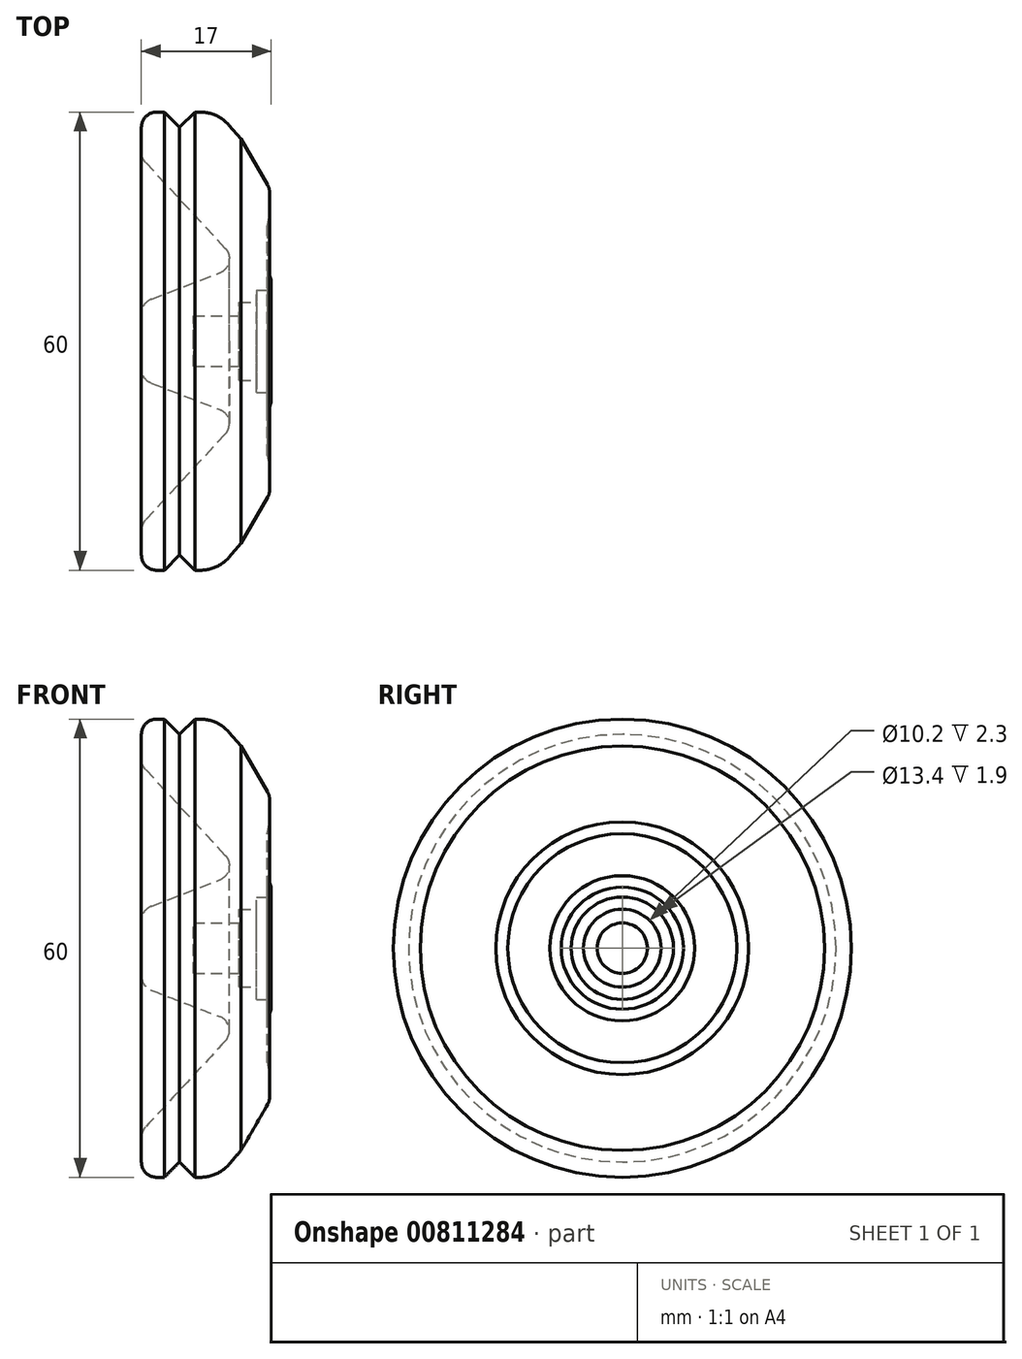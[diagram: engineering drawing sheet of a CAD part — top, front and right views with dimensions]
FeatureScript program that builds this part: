
annotation { "Feature Type Name" : "Feature", "Feature Type Description" : "" }
export const myFeature = defineFeature(function(context is Context, id is Id, definition is map)
    precondition{}
    {
        {
            var Q0;
            Q0=qCreatedBy(makeId("Front.planeOp"),FACE);
            var sketch = newSketch(context, id + "F0", { "sketchPlane" : qUnion([Q0])});
            skLineSegment(sketch, "E0", {"start": v(2, 30) * mm, "end": v(3, 30) * mm});
            skLineSegment(sketch, "E1", {"start": v(3, 30) * mm, "end": v(5, 28) * mm});
            skLineSegment(sketch, "E2", {"start": v(5, 28) * mm, "end": v(7, 30) * mm});
            skLineSegment(sketch, "E3", {"start": v(15.1, 5.1) * mm, "end": v(12.8, 5.1) * mm});
            skLineSegment(sketch, "E4", {"start": v(12.8, 5.1) * mm, "end": v(12.8, 3.3) * mm});
            skLineSegment(sketch, "E5", {"start": v(12.8, 3.3) * mm, "end": v(6.8, 3.3) * mm});
            skLineSegment(sketch, "E6", {"start": v(6.8, 3.3) * mm, "end": v(6.8, 0) * mm});
            skLineSegment(sketch, "E7", {"start": v(6.8, 0) * mm, "end": v(0, 0) * mm});
            skPoint(sketch, "E8.visualSharp", {"position": v(0, 30) * mm});
            skLineSegment(sketch, "E9", {"start": v(15.1, 5.1) * mm, "end": v(15.1, 6.7) * mm});
            skLineSegment(sketch, "E10", {"start": v(15.1, 6.7) * mm, "end": v(17, 6.7) * mm});
            skLineSegment(sketch, "E11", {"start": v(17, 6.7) * mm, "end": v(17, 8) * mm});
            skLineSegment(sketch, "E12", {"start": v(16.5, 15) * mm, "end": v(16.5, 9.5) * mm});
            skLineSegment(sketch, "E13", {"start": v(16.5, 9.5) * mm, "end": v(17, 8) * mm});
            skLineSegment(sketch, "E14", {"start": v(0, 3.63) * mm, "end": v(0, 0) * mm});
            skLineSegment(sketch, "E15", {"start": v(16.8, 16.55) * mm, "end": v(16.5, 15) * mm});
            skPoint(sketch, "E16.visualSharp", {"position": v(16.8, 20) * mm});
            skPoint(sketch, "E17.visualSharp", {"position": v(0, 24) * mm});
            skLineSegment(sketch, "E18", {"start": v(7, 30) * mm, "end": v(7.72, 30) * mm});
            skLineSegment(sketch, "E19", {"start": v(11.5, 28.28) * mm, "end": v(13.06, 26.48) * mm});
            skLineSegment(sketch, "E20", {"start": v(13.06, 26.48) * mm, "end": v(16.53, 20.46) * mm});
            skLineSegment(sketch, "E21", {"start": v(16.8, 16.55) * mm, "end": v(16.8, 19.46) * mm});
            skPoint(sketch, "E22.visualSharp", {"position": v(10, 30) * mm});
            skLineSegment(sketch, "E23", {"start": v(0, 28) * mm, "end": v(0, 24.79) * mm});
            skPoint(sketch, "E24.visualSharp", {"position": v(0, 5) * mm});
            skPoint(sketch, "E25.visualSharp", {"position": v(13, 10) * mm});
            skLineSegment(sketch, "E26", {"start": v(10.99, 12.17) * mm, "end": v(0.53, 23.42) * mm});
            skLineSegment(sketch, "E27", {"start": v(1.28, 5.5) * mm, "end": v(10.24, 8.94) * mm});
            skArc(sketch, "E28.filletArc", {"start": v(2, 30) * mm, "mid": v(0.59, 29.41) * mm, "end": v(0, 28) * mm});
            skArc(sketch, "E29.filletArc", {"start": v(11.5, 28.28) * mm, "mid": v(9.8, 29.55) * mm, "end": v(7.72, 30) * mm});
            skArc(sketch, "E30.filletArc", {"start": v(16.8, 19.46) * mm, "mid": v(16.73, 19.98) * mm, "end": v(16.53, 20.46) * mm});
            skArc(sketch, "E31.filletArc", {"start": v(0, 24.79) * mm, "mid": v(0.14, 24.05) * mm, "end": v(0.53, 23.42) * mm});
            skArc(sketch, "E32.filletArc", {"start": v(10.24, 8.94) * mm, "mid": v(11.47, 10.35) * mm, "end": v(10.99, 12.17) * mm});
            skArc(sketch, "E33.filletArc", {"start": v(1.28, 5.5) * mm, "mid": v(0.35, 4.76) * mm, "end": v(0, 3.63) * mm});
            skSolve(sketch);
        }
        {
            var Q0;
            Q0=makeQuery(id+"F0.imprint","IMPRINT",FACE,{"disambiguationData":[TD([[makeQuery(id+"F0.imprint","IMPRINT",EDGE,{"derivedFrom":sQuery(id+"F0.wireOp",EDGE,"E0")}),-1.0]])]});
            var Q1;
            Q1=sQuery(id+"F0.wireOp",EDGE,"E7");
            revolve(context, id + "F1", {"surfaceOperationType" : NewSurfaceOperationType.NEW, "entities" : qUnion([Q0]), "axis" : qUnion([Q1]), "revolveType" : RevolveType.FULL});
        }
    });
